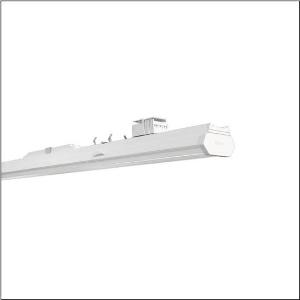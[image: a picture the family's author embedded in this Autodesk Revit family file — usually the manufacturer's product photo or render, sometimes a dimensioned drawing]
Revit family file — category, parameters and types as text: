
# Revit family: licross_r__21_protected_mo_52ts12dne7xf_c152
name_source: partatom
category: Lighting Fixtures
units: mm (PartAtom-declared; Revit-internal decimal feet)

## family parameters
Cut with Voids When Loaded = No
Host = Face
Light Source = No
Part Type = Normal
Room Calculation Point = No
Round Connector Dimension = Use Diameter
Shared = No

## types (1)
- --- (1 x LED, 7250 lm, 60.9 W, 5000K)
    Apparent Load = 61 VA
    CIE Flux Codes = 54 82 95 97 100
    Color Rendering = 90
    Color Temperature = 5000K
    Default Elevation = 1800 mm
    Description = Licross® 21 Protected MO, luminaire insert, of sheet steel, galvanised, coil coated, white, length: 1.500mm, width: 90mm, height: 101mm, LED rated luminous flux: 7.250lm, light colour: 950, control gear: DALI 2, control gear: ECG DALI, with plug, 5-pole, with phase selection, mains connection: 220..240V, AC, 50/60Hz, rated input power: 61W, halogen-free wiring, primary optical cover: cover, of PMMA, light emission: direct distribution, primary light characteristic: symmetric, protection rating (complete): IP50, insulation class (complete): insulation class I (protective earthing), certification: CE, ENEC, VDE, UKCA, protection symbol: D if used in an environment with non-conductive dust loads with corresponding accessories, impact resistance: IK06, permissible ambient temperature for indoor applications: -25..+40°C, corresponds to IFS (International Featured Standards) requirements for safety and quality in the food industry, reducing of maximum allowable ambient temperature of 5°C with ceiling mounting, LABS conformity tested according to VDMA 24364:2018-05, packaging unit: 1 piece
    Height = 92 mm
    Lamp = 1 x LED
    Lamp Light Flux = 7250 lm
    Lamp Power = 60.9 W
    Lamp count = 1
    Length = 1500 mm
    Luminous efficacy = 119 lm/W
    Manufacturer = Siteco
    ModVariant = No
    Model = 52TS12DNE7XF
    Mounting Place = Ceiling
    Mounting Type = Pendant
    Number of Poles = 1
    OnlyDefault = Yes
    Power Factor = 1
    Product Name = Licross® 21 Protected MO
    Product group = luminaire insert
    ProductGroupID = 901
    Protection Class = Protection class I
    Protection Degree = IP 50
    RLX_Detail_Level = 1
    RLX_Emergency_Light_Flux = 0 lm
    RLX_Emergency_Type = 0
    RLX_Emergency_Type_DB = No
    RlxData = <blob elided: 24273 chars, md5=0f0cd17f>
    Socket = socket
    Standby Power = 0 W
    System Light Flux = 7250 lm
    System Power = 61 W
    Type Comments = factory setting: luminous flux: 100 % | dim-lin: 254 | 405 mA
    Type Image = l_1256145.jpg
    URL = http://relux.com
    VarID = @adj_136569
    Voltage = 0 V
    Weight = 0.00 kg
    Width = 88 mm

## geometry (parser evidence)
native form markers: Blend x4, Sweep x12
no freeform markers — native parametric forms only
